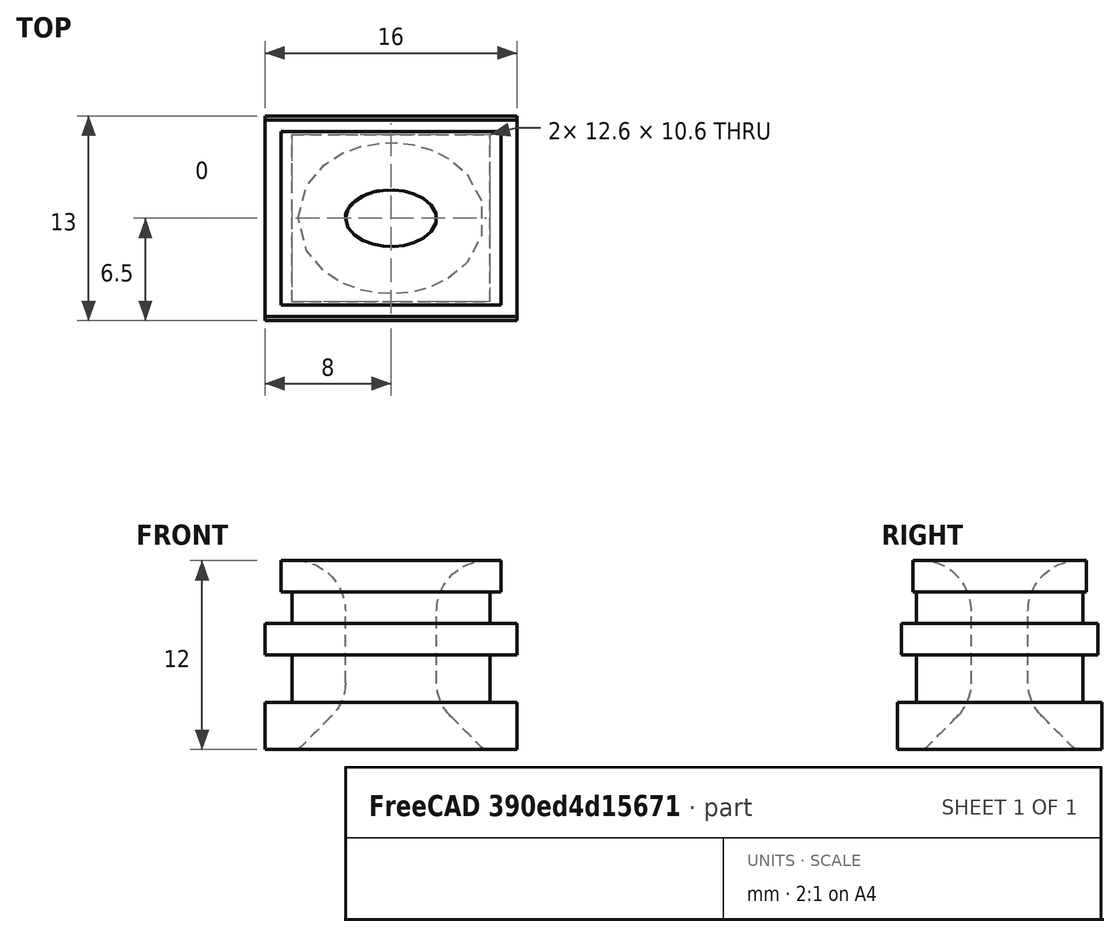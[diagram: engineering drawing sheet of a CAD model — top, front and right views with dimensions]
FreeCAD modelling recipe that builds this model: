
FCSTD DOCUMENT  (FreeCAD 0.19R0.19.2)
Label: 04
License: All rights reserved
LicenseURL: http://en.wikipedia.org/wiki/All_rights_reserved
objects: Part::Box×5, Sketcher::SketchObject×3, Part::Fillet×2, Part::MultiFuse×1, Part::Extrusion×1, Part::Cut×1, Part::Chamfer×1
note: 14 computed .brp shape members not serialized (recipe doc carries the construction recipe); baked Part::Feature solids carry a one-line shape summary decoded from their .brp

FEATURE [Sketcher::SketchObject] Sketch
  FullyConstrained = true
FEATURE [Part::Box] Box  label="Cube"
  AttacherType = Attacher::AttachEngine3D
  Height = 3
  Length = 12.6
  Placement = pos=(1.7,1.2,3) rot=(0,0,1;0rad)
  Width = 10.6
FEATURE [Part::Box] Box001  label="Cube001"
  AttacherType = Attacher::AttachEngine3D
  Height = 3
  Length = 16
  Width = 13
FEATURE [Part::Box] Box002  label="Cube002"
  AttacherType = Attacher::AttachEngine3D
  Height = 2
  Length = 16
  Placement = pos=(0,0.25,6) rot=(0,0,1;0rad)
  Width = 12.5
FEATURE [Part::Box] Box003  label="Cube003"
  AttacherType = Attacher::AttachEngine3D
  Height = 2
  Length = 12.6
  Placement = pos=(1.7,1.2,8) rot=(0,0,1;0rad)
  Width = 10.6
FEATURE [Part::Box] Box004  label="Cube004"
  AttacherType = Attacher::AttachEngine3D
  Height = 2
  Length = 14
  Placement = pos=(1,1,10) rot=(0,0,1;0rad)
  Width = 11
FEATURE [Part::MultiFuse] Fusion
  Shapes = -> [Box004,Box003,Box002,Box,Box001]
FEATURE [Sketcher::SketchObject] Sketch001
  FullyConstrained = true
  MapMode = 5
  Placement = pos=(0,0,12) rot=(0,0,1;0rad)
  Support = -> [Fusion]
FEATURE [Sketcher::SketchObject] Sketch002
  FullyConstrained = true
  MapMode = 5
  Placement = pos=(0,0,12) rot=(0,0,1;0rad)
  Support = -> [Fusion]
  sketch-geometry (5):
    g0: Ellipse CenterX=1e-16 CenterY=0 CenterZ=0 NormalX=0 NormalY=0 NormalZ=1 MajorRadius=2.9 MinorRadius=1.8 AngleXU=-3.14159
    g1: LineSegment StartX=-2.9 StartY=0 StartZ=0 EndX=2.9 EndY=0 EndZ=0
    g2: LineSegment StartX=1e-16 StartY=-1.8 StartZ=0 EndX=1e-16 EndY=1.8 EndZ=0
    g3: GeomPoint X=-2.27376 Y=0 Z=0
    g4: GeomPoint X=2.27376 Y=0 Z=0
  constraints (2):
    c: InternalAlignment(g1-g4 -> g0) x4
    c: Block(g0)
FEATURE [Part::Extrusion] Extrude
  Base = -> Sketch002
  Dir = (0,0,1)
  DirMode = 2
  FaceMakerClass = Part::FaceMakerBullseye
  LengthFwd = 14
  LengthRev = 0
  Placement = pos=(8,6.5,-13) rot=(0,0,1;0rad)
  Solid = true
  Symmetric = false
FEATURE [Part::Cut] Cut
  Base = -> Fusion
  Tool = -> Extrude
FEATURE [Part::Fillet] Fillet
  Base = -> Cut
  Edges = 1 edges r=3.2: [Edge10]
FEATURE [Part::Chamfer] Chamfer
  Base = -> Fillet
  Edges = 1 edges r=3: [Edge17]
FEATURE [Part::Fillet] Fillet001
  Base = -> Chamfer
  Edges = 1 edges r=3: [Edge2]
